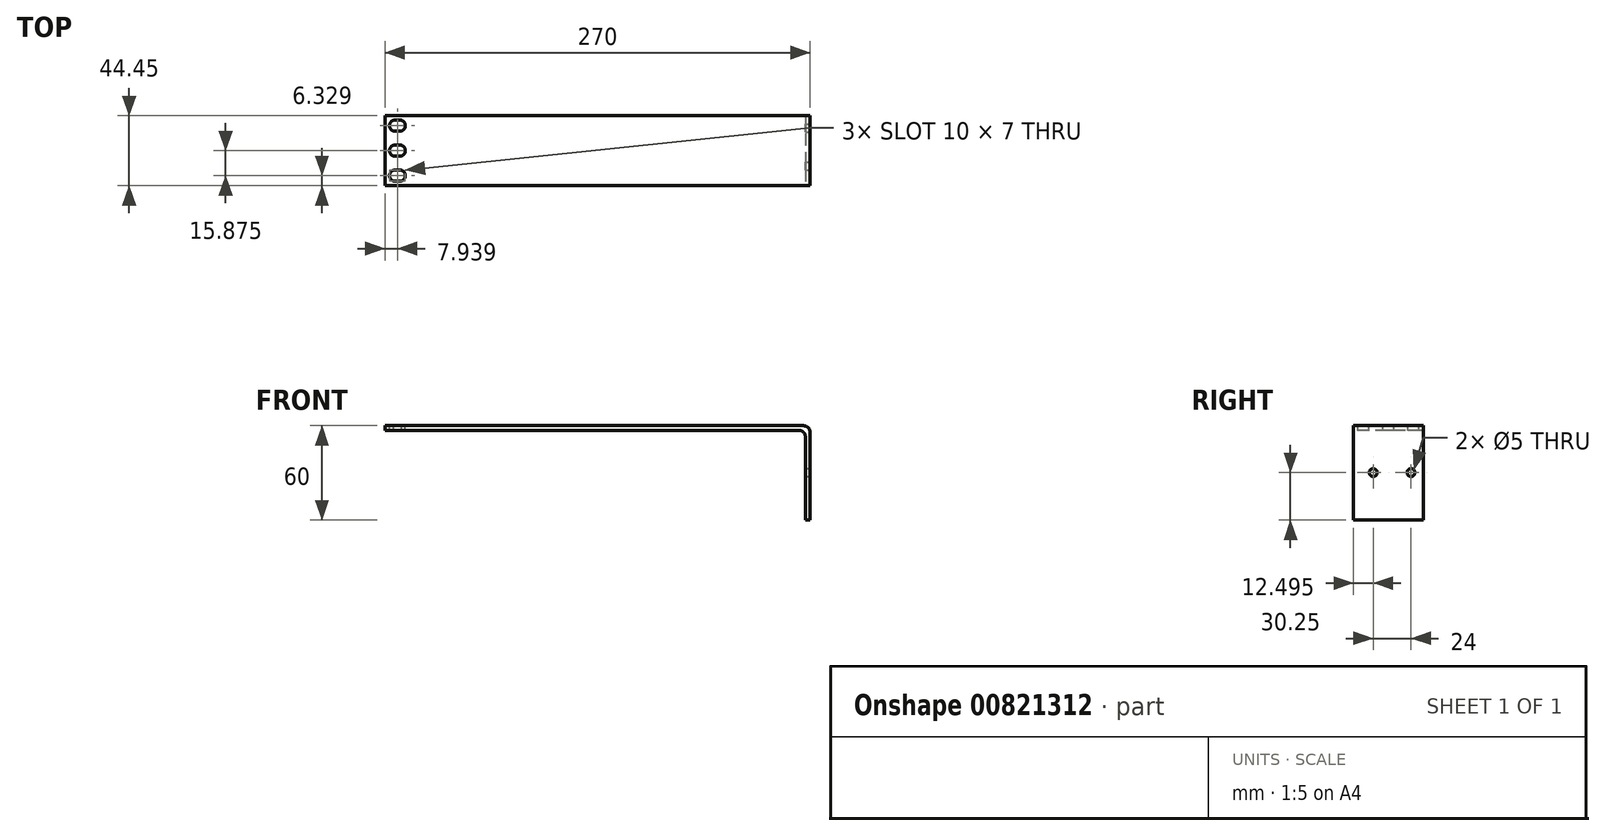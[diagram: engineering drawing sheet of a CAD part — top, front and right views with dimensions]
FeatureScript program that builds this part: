
annotation { "Feature Type Name" : "Feature", "Feature Type Description" : "" }
export const myFeature = defineFeature(function(context is Context, id is Id, definition is map)
    precondition{}
    {
        {
            var Q0;
            Q0=qCreatedBy(makeId("Top.planeOp"),FACE);
            var sketch = newSketch(context, id + "F0", { "sketchPlane" : qUnion([Q0])});
            skLineSegment(sketch, "E0.bottom", {"start": v(-66.95, 7.9) * mm, "end": v(203.05, 7.9) * mm});
            skLineSegment(sketch, "E0.top", {"start": v(-66.95, -36.55) * mm, "end": v(203.05, -36.55) * mm});
            skLineSegment(sketch, "E0.left", {"start": v(-66.95, 7.9) * mm, "end": v(-66.95, -36.55) * mm});
            skLineSegment(sketch, "E0.right", {"start": v(203.05, 7.9) * mm, "end": v(203.05, -36.55) * mm});
            skSolve(sketch);
        }
        {
            var Q0;
            Q0=makeQuery(id+"F0.imprint","IMPRINT",FACE,{"disambiguationData":[TD([[makeQuery(id+"F0.imprint","IMPRINT",EDGE,{"derivedFrom":sQuery(id+"F0.wireOp",EDGE,"E0.bottom")}),-1.0]])]});
            extrude(context, id + "F1", {"entities" : qUnion([Q0]), "depth" : 3 * mm, "offsetDistance" : 25 * mm});
        }
        {
            var Q0;
            Q0=makeQuery(id+"F1.opExtrude","CAP_FACE",FACE,{"disambiguationData":[OSD([sQuery(id+"F0.wireOp",EDGE,"E0.bottom"),sQuery(id+"F0.wireOp",EDGE,"E0.top"),sQuery(id+"F0.wireOp",EDGE,"E0.left"),sQuery(id+"F0.wireOp",EDGE,"E0.right")])],"isStart":false});
            var sketch = newSketch(context, id + "F2", { "sketchPlane" : qUnion([Q0])});
            skLineSegment(sketch, "E1.MirrorCS", {"start": v(-59.01, -1.97) * mm, "end": v(-61.51, -1.97) * mm});
            skLineSegment(sketch, "E2.MirrorCS", {"start": v(-59.01, -17.85) * mm, "end": v(-61.51, -17.85) * mm});
            skLineSegment(sketch, "E3.MirrorCS", {"start": v(-59.01, -17.85) * mm, "end": v(-56.51, -17.85) * mm});
            skLineSegment(sketch, "E4.MirrorCS", {"start": v(-59.01, -10.85) * mm, "end": v(-56.51, -10.85) * mm});
            skLineSegment(sketch, "E5.MirrorCS", {"start": v(-59.01, -10.85) * mm, "end": v(-61.51, -10.85) * mm});
            skLineSegment(sketch, "E6.MirrorCS", {"start": v(-59.01, -1.97) * mm, "end": v(-56.51, -1.97) * mm});
            skLineSegment(sketch, "E7.MirrorCS", {"start": v(-59.01, 5.03) * mm, "end": v(-61.51, 5.03) * mm});
            skLineSegment(sketch, "E8.MirrorCS", {"start": v(-59.01, 5.03) * mm, "end": v(-56.51, 5.03) * mm});
            skArc(sketch, "E9.MirrorCS", {"start": v(-61.51, -17.85) * mm, "mid": v(-64.01, -14.35) * mm, "end": v(-61.51, -10.85) * mm});
            skPoint(sketch, "E10.MirrorP", {"position": v(-59.01, 1.55) * mm});
            skPoint(sketch, "E11.MirrorP", {"position": v(-59.01, -14.33) * mm});
            skLineSegment(sketch, "E12.MirrorCS", {"start": v(-59.01, -26.72) * mm, "end": v(-56.51, -26.72) * mm});
            skPoint(sketch, "E13.MirrorP", {"position": v(-59.01, 1.53) * mm});
            skLineSegment(sketch, "E14.MirrorCS", {"start": v(-59.01, -26.72) * mm, "end": v(-61.51, -26.72) * mm});
            skArc(sketch, "E15.MirrorCS", {"start": v(-56.51, -10.85) * mm, "mid": v(-54.01, -14.35) * mm, "end": v(-56.51, -17.85) * mm});
            skArc(sketch, "E16.MirrorCS", {"start": v(-56.51, -1.97) * mm, "mid": v(-54.01, 1.53) * mm, "end": v(-56.51, 5.03) * mm});
            skPoint(sketch, "E17.MirrorP", {"position": v(-59.01, -30.22) * mm});
            skLineSegment(sketch, "E18.MirrorCS", {"start": v(-59.01, -33.72) * mm, "end": v(-56.51, -33.72) * mm});
            skPoint(sketch, "E19.MirrorP", {"position": v(-59.01, -14.35) * mm});
            skLineSegment(sketch, "E20.MirrorCS", {"start": v(-59.01, -33.72) * mm, "end": v(-61.51, -33.72) * mm});
            skArc(sketch, "E21.MirrorCS", {"start": v(-61.51, 5.03) * mm, "mid": v(-64.01, 1.53) * mm, "end": v(-61.51, -1.97) * mm});
            skPoint(sketch, "E22.MirrorP", {"position": v(-59.01, -30.2) * mm});
            skArc(sketch, "E23.MirrorCS", {"start": v(-56.51, -33.72) * mm, "mid": v(-54.01, -30.22) * mm, "end": v(-56.51, -26.72) * mm});
            skArc(sketch, "E24.MirrorCS", {"start": v(-61.51, -26.72) * mm, "mid": v(-64.01, -30.22) * mm, "end": v(-61.51, -33.72) * mm});
            skLineSegment(sketch, "E25", {"start": v(-51.07, 7.9) * mm, "end": v(-51.07, -36.55) * mm});
            skLineSegment(sketch, "E26", {"start": v(200.05, 7.9) * mm, "end": v(200.05, -36.55) * mm});
            skSolve(sketch);
        }
        {
            var Q0;
            Q0=makeQuery(id+"F2.imprint","IMPRINT",FACE,{"disambiguationData":[TD([[makeQuery(id+"F2.imprint","IMPRINT",EDGE,{"derivedFrom":sQuery(id+"F2.wireOp",EDGE,"E12.MirrorCS")}),-1.0]])]});
            var Q1;
            Q1=makeQuery(id+"F2.imprint","IMPRINT",FACE,{"disambiguationData":[TD([[makeQuery(id+"F2.imprint","IMPRINT",EDGE,{"derivedFrom":sQuery(id+"F2.wireOp",EDGE,"E28.MirrorCS")}),1.0]])]});
            var Q2;
            Q2=makeQuery(id+"F2.imprint","IMPRINT",FACE,{"disambiguationData":[TD([[makeQuery(id+"F2.imprint","IMPRINT",EDGE,{"derivedFrom":sQuery(id+"F2.wireOp",EDGE,"E34.MirrorCS")}),-1.0]])]});
            var Q3;
            Q3=makeQuery(id+"F2.imprint","IMPRINT",FACE,{"disambiguationData":[TD([[makeQuery(id+"F2.imprint","IMPRINT",EDGE,{"derivedFrom":sQuery(id+"F2.wireOp",EDGE,"E2.MirrorCS")}),-1.0]])]});
            var Q4;
            Q4=makeQuery(id+"F2.imprint","IMPRINT",FACE,{"disambiguationData":[TD([[makeQuery(id+"F2.imprint","IMPRINT",EDGE,{"derivedFrom":sQuery(id+"F2.wireOp",EDGE,"E1.MirrorCS")}),-1.0]])]});
            var Q5;
            Q5=makeQuery(id+"F2.imprint","IMPRINT",FACE,{"disambiguationData":[TD([[makeQuery(id+"F2.imprint","IMPRINT",EDGE,{"derivedFrom":sQuery(id+"F2.wireOp",EDGE,"e643efc0-838d-4c4d-bbf6-0098947567ab37.MirrorCS")}),1.0]])]});
            var Q6;
            Q6=makeQuery(id+"F2.imprint","IMPRINT",FACE,{"disambiguationData":[TD([[makeQuery(id+"F2.imprint","IMPRINT",EDGE,{"derivedFrom":sQuery(id+"F2.wireOp",EDGE,"E243.MirrorC")}),1.0]])]});
            var Q7;
            Q7=makeQuery(id+"F2.imprint","IMPRINT",FACE,{"disambiguationData":[TD([[makeQuery(id+"F2.imprint","IMPRINT",EDGE,{"derivedFrom":sQuery(id+"F2.wireOp",EDGE,"E79.MirrorC")}),-1.0]])]});
            var Q8;
            Q8=makeQuery(id+"F2.imprint","IMPRINT",FACE,{"disambiguationData":[TD([[makeQuery(id+"F2.imprint","IMPRINT",EDGE,{"derivedFrom":sQuery(id+"F2.wireOp",EDGE,"E94.MirrorC")}),-1.0]])]});
            var Q9;
            Q9=makeQuery(id+"F2.imprint","IMPRINT",FACE,{"disambiguationData":[TD([[makeQuery(id+"F2.imprint","IMPRINT",EDGE,{"derivedFrom":sQuery(id+"F2.wireOp",EDGE,"E229.MirrorC")}),-1.0]])]});
            var Q10;
            Q10=makeQuery(id+"F2.imprint","IMPRINT",FACE,{"disambiguationData":[TD([[makeQuery(id+"F2.imprint","IMPRINT",EDGE,{"derivedFrom":sQuery(id+"F2.wireOp",EDGE,"E288.MirrorC")}),1.0]])]});
            var Q11;
            Q11=makeQuery(id+"F2.imprint","IMPRINT",FACE,{"disambiguationData":[TD([[makeQuery(id+"F2.imprint","IMPRINT",EDGE,{"derivedFrom":sQuery(id+"F2.wireOp",EDGE,"E293.MirrorC")}),1.0]])]});
            var Q12;
            Q12=makeQuery(id+"F2.imprint","IMPRINT",FACE,{"disambiguationData":[TD([[makeQuery(id+"F2.imprint","IMPRINT",EDGE,{"derivedFrom":sQuery(id+"F2.wireOp",EDGE,"E263.MirrorC")}),-1.0]])]});
            var Q13;
            Q13=makeQuery(id+"F2.imprint","IMPRINT",FACE,{"disambiguationData":[TD([[makeQuery(id+"F2.imprint","IMPRINT",EDGE,{"derivedFrom":sQuery(id+"F2.wireOp",EDGE,"E65.MirrorC")}),-1.0]])]});
            var Q14;
            Q14=makeQuery(id+"F2.imprint","IMPRINT",FACE,{"disambiguationData":[TD([[makeQuery(id+"F2.imprint","IMPRINT",EDGE,{"derivedFrom":sQuery(id+"F2.wireOp",EDGE,"E71.MirrorC")}),-1.0]])]});
            var Q15;
            Q15=makeQuery(id+"F2.imprint","IMPRINT",FACE,{"disambiguationData":[TD([[makeQuery(id+"F2.imprint","IMPRINT",EDGE,{"derivedFrom":sQuery(id+"F2.wireOp",EDGE,"E92.MirrorC")}),-1.0]])]});
            var Q16;
            Q16=makeQuery(id+"F2.imprint","IMPRINT",FACE,{"disambiguationData":[TD([[makeQuery(id+"F2.imprint","IMPRINT",EDGE,{"derivedFrom":sQuery(id+"F2.wireOp",EDGE,"E306.MirrorC")}),-1.0]])]});
            var Q17;
            Q17=makeQuery(id+"F2.imprint","IMPRINT",FACE,{"disambiguationData":[TD([[makeQuery(id+"F2.imprint","IMPRINT",EDGE,{"derivedFrom":sQuery(id+"F2.wireOp",EDGE,"E87.MirrorC")}),-1.0]])]});
            var Q18;
            Q18=makeQuery(id+"F2.imprint","IMPRINT",FACE,{"disambiguationData":[TD([[makeQuery(id+"F2.imprint","IMPRINT",EDGE,{"derivedFrom":sQuery(id+"F2.wireOp",EDGE,"E68.MirrorC")}),1.0]])]});
            var Q19;
            Q19=makeQuery(id+"F2.imprint","IMPRINT",FACE,{"disambiguationData":[TD([[makeQuery(id+"F2.imprint","IMPRINT",EDGE,{"derivedFrom":sQuery(id+"F2.wireOp",EDGE,"E224.MirrorC")}),1.0]])]});
            var Q20;
            Q20=makeQuery(id+"F2.imprint","IMPRINT",FACE,{"disambiguationData":[TD([[makeQuery(id+"F2.imprint","IMPRINT",EDGE,{"derivedFrom":sQuery(id+"F2.wireOp",EDGE,"E85.MirrorC")}),1.0]])]});
            var Q21;
            Q21=makeQuery(id+"F2.imprint","IMPRINT",FACE,{"disambiguationData":[TD([[makeQuery(id+"F2.imprint","IMPRINT",EDGE,{"derivedFrom":sQuery(id+"F2.wireOp",EDGE,"E302.MirrorC")}),-1.0]])]});
            var Q22;
            Q22=makeQuery(id+"F2.imprint","IMPRINT",FACE,{"disambiguationData":[TD([[makeQuery(id+"F2.imprint","IMPRINT",EDGE,{"derivedFrom":sQuery(id+"F2.wireOp",EDGE,"E289.MirrorC")}),1.0]])]});
            var Q23;
            Q23=makeQuery(id+"F2.imprint","IMPRINT",FACE,{"disambiguationData":[TD([[makeQuery(id+"F2.imprint","IMPRINT",EDGE,{"derivedFrom":sQuery(id+"F2.wireOp",EDGE,"E228.MirrorC")}),-1.0]])]});
            var Q24;
            Q24=makeQuery(id+"F2.imprint","IMPRINT",FACE,{"disambiguationData":[TD([[makeQuery(id+"F2.imprint","IMPRINT",EDGE,{"derivedFrom":sQuery(id+"F2.wireOp",EDGE,"E95.MirrorC")}),1.0]])]});
            var Q25;
            Q25=makeQuery(id+"F2.imprint","IMPRINT",FACE,{"disambiguationData":[TD([[makeQuery(id+"F2.imprint","IMPRINT",EDGE,{"derivedFrom":sQuery(id+"F2.wireOp",EDGE,"E264.MirrorC")}),-1.0]])]});
            var Q26;
            Q26=makeQuery(id+"F2.imprint","IMPRINT",FACE,{"disambiguationData":[TD([[makeQuery(id+"F2.imprint","IMPRINT",EDGE,{"derivedFrom":sQuery(id+"F2.wireOp",EDGE,"E72.MirrorC")}),1.0]])]});
            var Q27;
            Q27=makeQuery(id+"F2.imprint","IMPRINT",FACE,{"disambiguationData":[TD([[makeQuery(id+"F2.imprint","IMPRINT",EDGE,{"derivedFrom":sQuery(id+"F2.wireOp",EDGE,"E296.MirrorC")}),1.0]])]});
            var Q28;
            Q28=makeQuery(id+"F2.imprint","IMPRINT",FACE,{"disambiguationData":[TD([[makeQuery(id+"F2.imprint","IMPRINT",EDGE,{"derivedFrom":sQuery(id+"F2.wireOp",EDGE,"E295.MirrorC")}),1.0]])]});
            var Q29;
            Q29=makeQuery(id+"F2.imprint","IMPRINT",FACE,{"disambiguationData":[TD([[makeQuery(id+"F2.imprint","IMPRINT",EDGE,{"derivedFrom":sQuery(id+"F2.wireOp",EDGE,"E248.MirrorC")}),-1.0]])]});
            var Q30;
            Q30=makeQuery(id+"F2.imprint","IMPRINT",FACE,{"disambiguationData":[TD([[makeQuery(id+"F2.imprint","IMPRINT",EDGE,{"derivedFrom":sQuery(id+"F2.wireOp",EDGE,"E82.MirrorC")}),-1.0]])]});
            var Q31;
            Q31=makeQuery(id+"F2.imprint","IMPRINT",FACE,{"disambiguationData":[TD([[makeQuery(id+"F2.imprint","IMPRINT",EDGE,{"derivedFrom":sQuery(id+"F2.wireOp",EDGE,"E299.MirrorC")}),1.0]])]});
            var Q32;
            Q32=makeQuery(id+"F2.imprint","IMPRINT",FACE,{"disambiguationData":[TD([[makeQuery(id+"F2.imprint","IMPRINT",EDGE,{"derivedFrom":sQuery(id+"F2.wireOp",EDGE,"E84.MirrorC")}),-1.0]])]});
            var Q33;
            Q33=makeQuery(id+"F2.imprint","IMPRINT",FACE,{"disambiguationData":[TD([[makeQuery(id+"F2.imprint","IMPRINT",EDGE,{"derivedFrom":sQuery(id+"F2.wireOp",EDGE,"E294.MirrorC")}),1.0]])]});
            var Q34;
            Q34=makeQuery(id+"F2.imprint","IMPRINT",FACE,{"disambiguationData":[TD([[makeQuery(id+"F2.imprint","IMPRINT",EDGE,{"derivedFrom":sQuery(id+"F2.wireOp",EDGE,"E241.MirrorC")}),-1.0]])]});
            var Q35;
            Q35=makeQuery(id+"F2.imprint","IMPRINT",FACE,{"disambiguationData":[TD([[makeQuery(id+"F2.imprint","IMPRINT",EDGE,{"derivedFrom":sQuery(id+"F2.wireOp",EDGE,"e643efc0-838d-4c4d-bbf6-0098947567ab93.MirrorC")}),-1.0]])]});
            var Q36;
            Q36=makeQuery(id+"F2.imprint","IMPRINT",FACE,{"disambiguationData":[TD([[makeQuery(id+"F2.imprint","IMPRINT",EDGE,{"derivedFrom":sQuery(id+"F2.wireOp",EDGE,"e643efc0-838d-4c4d-bbf6-0098947567ab87.MirrorC")}),1.0]])]});
            var Q37;
            Q37=makeQuery(id+"F2.imprint","IMPRINT",FACE,{"disambiguationData":[TD([[makeQuery(id+"F2.imprint","IMPRINT",EDGE,{"derivedFrom":sQuery(id+"F2.wireOp",EDGE,"e643efc0-838d-4c4d-bbf6-0098947567ab92.MirrorC")}),-1.0]])]});
            var Q38;
            Q38=makeQuery(id+"F2.imprint","IMPRINT",FACE,{"disambiguationData":[TD([[makeQuery(id+"F2.imprint","IMPRINT",EDGE,{"derivedFrom":sQuery(id+"F2.wireOp",EDGE,"e643efc0-838d-4c4d-bbf6-0098947567ab98.MirrorC")}),-1.0]])]});
            var Q39;
            Q39=makeQuery(id+"F2.imprint","IMPRINT",FACE,{"disambiguationData":[TD([[makeQuery(id+"F2.imprint","IMPRINT",EDGE,{"derivedFrom":sQuery(id+"F2.wireOp",EDGE,"E207.MirrorC")}),-1.0]])]});
            var Q40;
            Q40=makeQuery(id+"F2.imprint","IMPRINT",FACE,{"disambiguationData":[TD([[makeQuery(id+"F2.imprint","IMPRINT",EDGE,{"derivedFrom":sQuery(id+"F2.wireOp",EDGE,"E62.MirrorC")}),1.0]])]});
            var Q41;
            Q41=makeQuery(id+"F2.imprint","IMPRINT",FACE,{"disambiguationData":[TD([[makeQuery(id+"F2.imprint","IMPRINT",EDGE,{"derivedFrom":sQuery(id+"F2.wireOp",EDGE,"e643efc0-838d-4c4d-bbf6-0098947567ab99.MirrorC")}),1.0]])]});
            var Q42;
            Q42=makeQuery(id+"F2.imprint","IMPRINT",FACE,{"disambiguationData":[TD([[makeQuery(id+"F2.imprint","IMPRINT",EDGE,{"derivedFrom":sQuery(id+"F2.wireOp",EDGE,"E202.MirrorC")}),-1.0]])]});
            var Q43;
            Q43=makeQuery(id+"F2.imprint","IMPRINT",FACE,{"disambiguationData":[TD([[makeQuery(id+"F2.imprint","IMPRINT",EDGE,{"derivedFrom":sQuery(id+"F2.wireOp",EDGE,"E98.MirrorC")}),1.0]])]});
            var Q44;
            Q44=makeQuery(id+"F2.imprint","IMPRINT",FACE,{"disambiguationData":[TD([[makeQuery(id+"F2.imprint","IMPRINT",EDGE,{"derivedFrom":sQuery(id+"F2.wireOp",EDGE,"E61.MirrorC")}),-1.0]])]});
            var Q45;
            Q45=makeQuery(id+"F2.imprint","IMPRINT",FACE,{"disambiguationData":[TD([[makeQuery(id+"F2.imprint","IMPRINT",EDGE,{"derivedFrom":sQuery(id+"F2.wireOp",EDGE,"E63.MirrorC")}),1.0]])]});
            var Q46;
            Q46=makeQuery(id+"F2.imprint","IMPRINT",FACE,{"disambiguationData":[TD([[makeQuery(id+"F2.imprint","IMPRINT",EDGE,{"derivedFrom":sQuery(id+"F2.wireOp",EDGE,"E301.MirrorC")}),1.0]])]});
            var Q47;
            Q47=makeQuery(id+"F2.imprint","IMPRINT",FACE,{"disambiguationData":[TD([[makeQuery(id+"F2.imprint","IMPRINT",EDGE,{"derivedFrom":sQuery(id+"F2.wireOp",EDGE,"e643efc0-838d-4c4d-bbf6-0098947567ab86.MirrorC")}),1.0]])]});
            var Q48;
            Q48=makeQuery(id+"F2.imprint","IMPRINT",FACE,{"disambiguationData":[TD([[makeQuery(id+"F2.imprint","IMPRINT",EDGE,{"derivedFrom":sQuery(id+"F2.wireOp",EDGE,"E206.MirrorC")}),-1.0]])]});
            var Q49;
            Q49=makeQuery(id+"F2.imprint","IMPRINT",FACE,{"disambiguationData":[TD([[makeQuery(id+"F2.imprint","IMPRINT",EDGE,{"derivedFrom":sQuery(id+"F2.wireOp",EDGE,"e643efc0-838d-4c4d-bbf6-0098947567ab88.MirrorC")}),1.0]])]});
            var Q50;
            Q50=makeQuery(id+"F2.imprint","IMPRINT",FACE,{"disambiguationData":[TD([[makeQuery(id+"F2.imprint","IMPRINT",EDGE,{"derivedFrom":sQuery(id+"F2.wireOp",EDGE,"E200.MirrorC")}),1.0]])]});
            var Q51;
            Q51=makeQuery(id+"F2.imprint","IMPRINT",FACE,{"disambiguationData":[TD([[makeQuery(id+"F2.imprint","IMPRINT",EDGE,{"derivedFrom":sQuery(id+"F2.wireOp",EDGE,"e643efc0-838d-4c4d-bbf6-0098947567ab91.MirrorC")}),1.0]])]});
            var Q52;
            Q52=makeQuery(id+"F2.imprint","IMPRINT",FACE,{"disambiguationData":[TD([[makeQuery(id+"F2.imprint","IMPRINT",EDGE,{"derivedFrom":sQuery(id+"F2.wireOp",EDGE,"E208.MirrorC")}),-1.0]])]});
            var Q53;
            Q53=makeQuery(id+"F2.imprint","IMPRINT",FACE,{"disambiguationData":[TD([[makeQuery(id+"F2.imprint","IMPRINT",EDGE,{"derivedFrom":sQuery(id+"F2.wireOp",EDGE,"E222.MirrorC")}),1.0]])]});
            var Q54;
            Q54=makeQuery(id+"F2.imprint","IMPRINT",FACE,{"disambiguationData":[TD([[makeQuery(id+"F2.imprint","IMPRINT",EDGE,{"derivedFrom":sQuery(id+"F2.wireOp",EDGE,"E40.MirrorCS")}),1.0]])]});
            var Q55;
            Q55=makeQuery(id+"F2.imprint","IMPRINT",FACE,{"disambiguationData":[TD([[makeQuery(id+"F2.imprint","IMPRINT",EDGE,{"derivedFrom":sQuery(id+"F2.wireOp",EDGE,"e643efc0-838d-4c4d-bbf6-0098947567ab3.MirrorCS")}),1.0]])]});
            var Q56;
            Q56=makeQuery(id+"F2.imprint","IMPRINT",FACE,{"disambiguationData":[TD([[makeQuery(id+"F2.imprint","IMPRINT",EDGE,{"derivedFrom":sQuery(id+"F2.wireOp",EDGE,"E26.MirrorCS")}),-1.0]])]});
            var Q57;
            Q57=makeQuery(id+"F2.imprint","IMPRINT",FACE,{"disambiguationData":[TD([[makeQuery(id+"F2.imprint","IMPRINT",EDGE,{"derivedFrom":sQuery(id+"F2.wireOp",EDGE,"e643efc0-838d-4c4d-bbf6-0098947567ab36.MirrorCS")}),-1.0]])]});
            var Q58;
            Q58=makeQuery(id+"F2.imprint","IMPRINT",FACE,{"disambiguationData":[TD([[makeQuery(id+"F2.imprint","IMPRINT",EDGE,{"derivedFrom":sQuery(id+"F2.wireOp",EDGE,"e643efc0-838d-4c4d-bbf6-0098947567ab6.MirrorCS")}),-1.0]])]});
            var Q59;
            Q59=makeQuery(id+"F2.imprint","IMPRINT",FACE,{"disambiguationData":[TD([[makeQuery(id+"F2.imprint","IMPRINT",EDGE,{"derivedFrom":sQuery(id+"F2.wireOp",EDGE,"e643efc0-838d-4c4d-bbf6-0098947567ab34.MirrorCS")}),1.0]])]});
            extrude(context, id + "F3", {"entities" : qUnion([Q0, Q1, Q2, Q3, Q4, Q5, Q6, Q7, Q8, Q9, Q10, Q11, Q12, Q13, Q14, Q15, Q16, Q17, Q18, Q19, Q20, Q21, Q22, Q23, Q24, Q25, Q26, Q27, Q28, Q29, Q30, Q31, Q32, Q33, Q34, Q35, Q36, Q37, Q38, Q39, Q40, Q41, Q42, Q43, Q44, Q45, Q46, Q47, Q48, Q49, Q50, Q51, Q52, Q53, Q54, Q55, Q56, Q57, Q58, Q59]), "operationType" : NewBodyOperationType.REMOVE, "oppositeDirection" : true, "depth" : 3 * mm, "offsetDistance" : 25 * mm});
        }
        {
            var Q0;
            {var subQ0=sQuery(id+"F2.wireOp",EDGE,"E26");Q0=makeQuery(id+"F2.imprint","IMPRINT",FACE,{"disambiguationData":[TD([[makeQuery(id+"F2.imprint","IMPRINT",EDGE,{"derivedFrom":subQ0}),1.0]])]});}
            extrude(context, id + "F4", {"entities" : qUnion([Q0]), "operationType" : NewBodyOperationType.ADD, "oppositeDirection" : true, "depth" : 60 * mm, "offsetDistance" : 25 * mm});
        }
        {
            var Q0;
            {var subQ0=sQuery(id+"F0.wireOp",EDGE,"E0.right");Q0=makeQuery(id+"F4.boolean.opBoolean","MERGE",FACE,{"derivedFrom":[makeQuery(id+"F1.opExtrude","SWEPT_FACE",FACE,{"disambiguationData":[OSD([subQ0])]}),makeQuery(id+"F4.opExtrude","SWEPT_FACE",FACE,{"disambiguationData":[OSD([subQ0])]})]});}
            var sketch = newSketch(context, id + "F5", { "sketchPlane" : qUnion([Q0])});
            skPoint(sketch, "E27", {"position": v(-24.05, -26.75) * mm});
            skPoint(sketch, "E28", {"position": v(-0.05, -26.75) * mm});
            skCircle(sketch, "E29", {"center": v(-24.05, -26.75) * mm, "radius": 2.5 * mm});
            skCircle(sketch, "E30", {"center": v(-0.05, -26.75) * mm, "radius": 2.5 * mm});
            skSolve(sketch);
        }
        {
            var Q0;
            Q0=makeQuery(id+"F5.imprint","IMPRINT",FACE,{"disambiguationData":[TD([[makeQuery(id+"F5.imprint","IMPRINT",EDGE,{"derivedFrom":sQuery(id+"F5.wireOp",EDGE,"E29")}),1.0]])]});
            var Q1;
            Q1=makeQuery(id+"F5.imprint","IMPRINT",FACE,{"disambiguationData":[TD([[makeQuery(id+"F5.imprint","IMPRINT",EDGE,{"derivedFrom":sQuery(id+"F5.wireOp",EDGE,"E30")}),1.0]])]});
            extrude(context, id + "F6", {"entities" : qUnion([Q0, Q1]), "operationType" : NewBodyOperationType.REMOVE, "oppositeDirection" : true, "depth" : 3 * mm, "offsetDistance" : 25 * mm});
        }
        {
            var Q0;
            Q0=makeQuery(id+"F4.boolean.opBoolean","INTERSECT",EDGE,{"derivedFrom":[makeQuery(id+"F1.opExtrude","CAP_FACE",FACE,{"disambiguationData":[OSD([sQuery(id+"F0.wireOp",EDGE,"E0.bottom"),sQuery(id+"F0.wireOp",EDGE,"E0.top"),sQuery(id+"F0.wireOp",EDGE,"E0.left"),sQuery(id+"F0.wireOp",EDGE,"E0.right")])],"isStart":true}),makeQuery(id+"F4.opExtrude","SWEPT_FACE",FACE,{"disambiguationData":[OSD([sQuery(id+"F2.wireOp",EDGE,"E26")])]})]});
            fillet(context, id + "F7", {"entities" : qUnion([Q0]), "radius" : 4 * mm, "tangentPropagation" : true, "allowEdgeOverflow" : false});
        }
        {
            var Q0;
            Q0=makeQuery(id+"F1.opExtrude","CAP_EDGE",EDGE,{"disambiguationData":[OSD([sQuery(id+"F0.wireOp",EDGE,"E0.right")])],"isStart":false});
            fillet(context, id + "F8", {"entities" : qUnion([Q0]), "radius" : 4 * mm, "tangentPropagation" : true, "allowEdgeOverflow" : false});
        }
    });
